# Revit family: 3532240
name_source: partatom
category: Lighting Fixtures
units: mm (PartAtom-declared; Revit-internal decimal feet)

## family parameters
Always vertical = Yes
Cut with Voids When Loaded = No
Light Source = No
Maintain Annotation Orientation = No
OmniClass Number = 23.80.70.14.21
OmniClass Title = Street and Roadway Lighting
Part Type = Normal
Room Calculation Point = No
Round Connector Dimension = Use Diameter
Shared = No
Work Plane-Based = No

## types (1)
- Standard
    Area = 0,59 m²
    Center of Gravity = X: -0,000 mm Y: -98,334 mm Z: 98,732 mm
    Default Elevation = 0 mm  [stored 0 ft]
    Density = 7860,00 kg/m³
    Description = VEGGBRAKETT C/C 240
    Design Status = 1
    Designer = sibj
    Filnamn-VO = L10082
    Manufacturer = Vik Ørsta AS
    Mass = 24,49 kg
    Model = 3532240
    Part Number = L10082
    Requested Accuracy = Low
    Size = 326mmX342mmX349,5mm
    Sti&Filnamn-VO = L10082
    Volume = 0,00 m³

note: [stored X ft] marks values corroborated as IEEE doubles in the binary element streams (Revit-internal decimal feet)

## geometry (parser evidence)
native form markers: Sweep x3
no freeform markers — native parametric forms only
